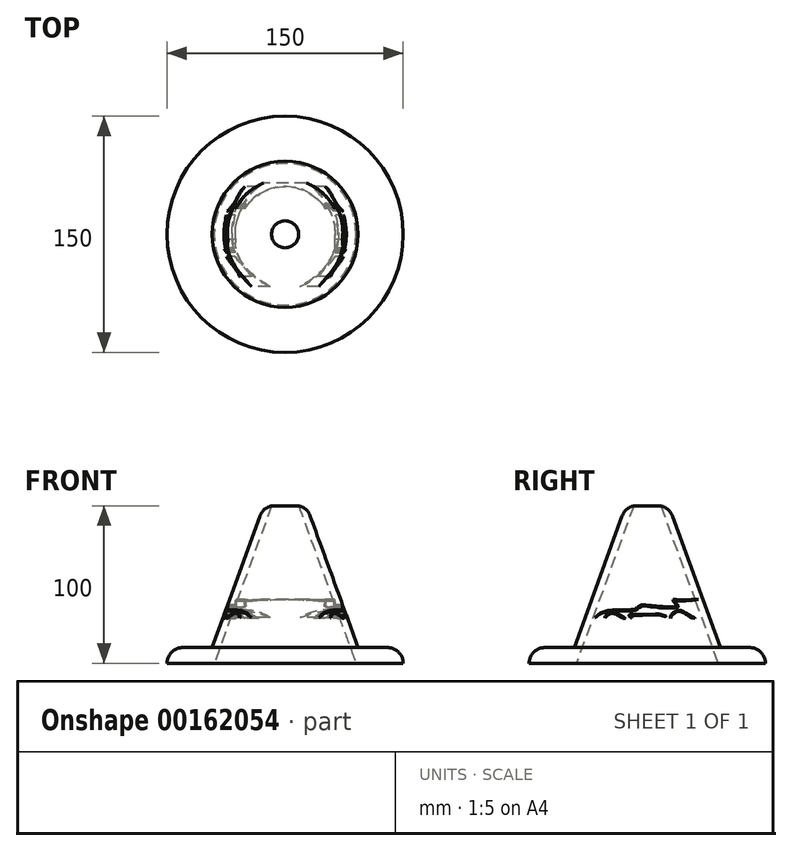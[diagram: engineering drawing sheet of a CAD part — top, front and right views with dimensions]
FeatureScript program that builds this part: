
annotation { "Feature Type Name" : "Feature", "Feature Type Description" : "" }
export const myFeature = defineFeature(function(context is Context, id is Id, definition is map)
    precondition{}
    {
        {
            var Q0;
            Q0=qCreatedBy(makeId("Top.planeOp"),FACE);
            var sketch = newSketch(context, id + "F0", { "sketchPlane" : qUnion([Q0])});
            skCircle(sketch, "E0", {"center": v(0, 0) * mm, "radius": 75 * mm});
            skCircle(sketch, "E1", {"center": v(0, 0) * mm, "radius": 50 * mm});
            skCircle(sketch, "E2", {"center": v(0, 0) * mm, "radius": 45 * mm});
            skSolve(sketch);
        }
        {
            var Q0;
            Q0=makeQuery(id+"F0.imprint","IMPRINT",FACE,{"disambiguationData":[TD([[makeQuery(id+"F0.imprint","IMPRINT",EDGE,{"derivedFrom":sQuery(id+"F0.wireOp",EDGE,"E1")}),1.0]])]});
            var Q1;
            Q1=makeQuery(id+"F0.imprint","IMPRINT",FACE,{"disambiguationData":[TD([[makeQuery(id+"F0.imprint","IMPRINT",EDGE,{"derivedFrom":sQuery(id+"F0.wireOp",EDGE,"E2")}),1.0]])]});
            extrude(context, id + "F1", {"entities" : qUnion([Q0, Q1]), "depth" : 100 * mm, "hasDraft" : true, "draftAngle" : 20 * degree, "draftPullDirection" : true});
        }
        {
            var Q0;
            Q0=makeQuery(id+"F0.imprint","IMPRINT",FACE,{"disambiguationData":[TD([[makeQuery(id+"F0.imprint","IMPRINT",EDGE,{"derivedFrom":sQuery(id+"F0.wireOp",EDGE,"E2")}),1.0]])]});
            extrude(context, id + "F2", {"entities" : qUnion([Q0]), "operationType" : NewBodyOperationType.REMOVE, "depth" : 100 * mm, "hasDraft" : true, "draftAngle" : 20 * degree, "draftPullDirection" : true});
        }
        {
            var Q0;
            Q0=makeQuery(id+"F0.imprint","IMPRINT",FACE,{"disambiguationData":[TD([[makeQuery(id+"F0.imprint","IMPRINT",EDGE,{"derivedFrom":sQuery(id+"F0.wireOp",EDGE,"E0")}),1.0]])]});
            extrude(context, id + "F3", {"entities" : qUnion([Q0]), "operationType" : NewBodyOperationType.ADD, "depth" : 10 * mm, "hasDraft" : true, "draftAngle" : 20 * degree});
        }
        {
            var Q0;
            Q0=qCreatedBy(makeId("Right.planeOp"),FACE);
            var sketch = newSketch(context, id + "F4", { "sketchPlane" : qUnion([Q0])});
            skFitSpline(sketch, "E3", {"points": [v(32.53, 40.55) * mm, v(25.34, 40.36) * mm, v(16.38, 40.45) * mm], "startDerivative": vector(-14.79, -0.53) * mm, "endDerivative": vector(-17.45, 0.33) * mm});
            skFitSpline(sketch, "E4", {"points": [v(16.38, 40.45) * mm, v(17.32, 38.3) * mm, v(18.56, 36.53) * mm, v(-3.24, 37.21) * mm], "startDerivative": vector(2.76, -10.76) * mm, "endDerivative": vector(-52.83, 6.04) * mm});
            skFitSpline(sketch, "E5", {"points": [v(-3.24, 37.21) * mm, v(-8.62, 34.1) * mm], "startDerivative": vector(-8.2, -2.54) * mm, "endDerivative": vector(-5.13, -1.28) * mm});
            skFitSpline(sketch, "E6", {"points": [v(-8.62, 34.1) * mm, v(-27.21, 32.98) * mm, v(-33.1, 29.01) * mm], "startDerivative": vector(-28.94, -1.2) * mm, "endDerivative": vector(-12.85, -12.83) * mm});
            skFitSpline(sketch, "E7", {"points": [v(-33.1, 29.01) * mm, v(-31.13, 30.46) * mm, v(-26.99, 32.35) * mm, v(-14.47, 33.16) * mm, v(-8.5, 33.27) * mm, v(-7.32, 33.68) * mm, v(-5.8, 34.8) * mm, v(-3.59, 36.38) * mm, v(-1.22, 36.42) * mm, v(5.34, 35.53) * mm, v(10.78, 35.12) * mm, v(16.15, 35.16) * mm, v(19.67, 36.12) * mm, v(18.26, 38.12) * mm, v(17.26, 39.68) * mm, v(17.63, 39.75) * mm, v(19.78, 39.75) * mm, v(26.11, 39.83) * mm, v(32.53, 40.55) * mm], "startDerivative": vector(41, 31.55) * mm, "endDerivative": vector(84.95, 12.19) * mm});
            skFitSpline(sketch, "E8", {"points": [v(-26.9, 28.68) * mm, v(-26.65, 29.87) * mm, v(-24.34, 31.91) * mm, v(-20.84, 32.3) * mm, v(-13.98, 28.55) * mm], "startDerivative": vector(0.28, 7.71) * mm, "endDerivative": vector(19.74, -13.19) * mm});
            skFitSpline(sketch, "E9", {"points": [v(-13.98, 28.55) * mm, v(-15.07, 28.55) * mm, v(-19.7, 31.01) * mm, v(-22.17, 31.68) * mm, v(-24.84, 30.86) * mm, v(-26.9, 28.68) * mm], "startDerivative": vector(-7.07, -1.8) * mm, "endDerivative": vector(-8.89, -11.8) * mm});
            skFitSpline(sketch, "E10", {"points": [v(-9.93, 28.66) * mm, v(-11, 29.76) * mm, v(-11.66, 30.3) * mm, v(-11.7, 30.86) * mm, v(-11.19, 30.97) * mm, v(7.29, 31.25) * mm, v(7.91, 31.17) * mm, v(12.27, 29.72) * mm, v(11.45, 29.68) * mm, v(8.46, 30.43) * mm, v(7.13, 30.58) * mm, v(-10.68, 30.39) * mm, v(-10.72, 30.35) * mm, v(-10.68, 30.15) * mm, v(-9.62, 28.97) * mm, v(-9.93, 28.66) * mm]});
            skFitSpline(sketch, "E11", {"points": [v(14.7, 28.62) * mm, v(14.74, 30) * mm, v(16.27, 31.88) * mm, v(18.86, 33.45) * mm, v(21.53, 33.37) * mm, v(30.31, 28.58) * mm], "startDerivative": vector(-1.44, 10.71) * mm, "endDerivative": vector(29.34, -17.99) * mm});
            skFitSpline(sketch, "E12", {"points": [v(14.7, 28.62) * mm, v(15.25, 29.68) * mm, v(16.66, 31.25) * mm, v(19.06, 32.78) * mm, v(22, 32.58) * mm, v(26.9, 29.68) * mm, v(28, 29.01) * mm, v(30.31, 28.58) * mm], "startDerivative": vector(4.6, 10.4) * mm, "endDerivative": vector(19.07, -2.6) * mm});
            skSolve(sketch);
        }
        {
            var Q0;
            Q0 = qSketchRegion(id + "F4", true);
            extrude(context, id + "F5", {"entities" : qUnion([Q0]), "operationType" : NewBodyOperationType.REMOVE, "depth" : 40 * mm, "hasSecondDirection" : true, "secondDirectionOppositeDirection" : true, "secondDirectionDepth" : 40 * mm});
        }
        {
            var Q0;
            Q0=makeQuery(id+"F1.opExtrude","CAP_EDGE",EDGE,{"disambiguationData":[OSD([sQuery(id+"F0.wireOp",EDGE,"E1")])],"isStart":false});
            var Q1;
            Q1=makeQuery(id+"F3.opExtrude","CAP_EDGE",EDGE,{"disambiguationData":[OSD([sQuery(id+"F0.wireOp",EDGE,"E0")])],"isStart":false});
            fillet(context, id + "F6", {"entities" : qUnion([Q0, Q1]), "radius" : 10 * mm, "tangentPropagation" : true, "allowEdgeOverflow" : false});
        }
    });
